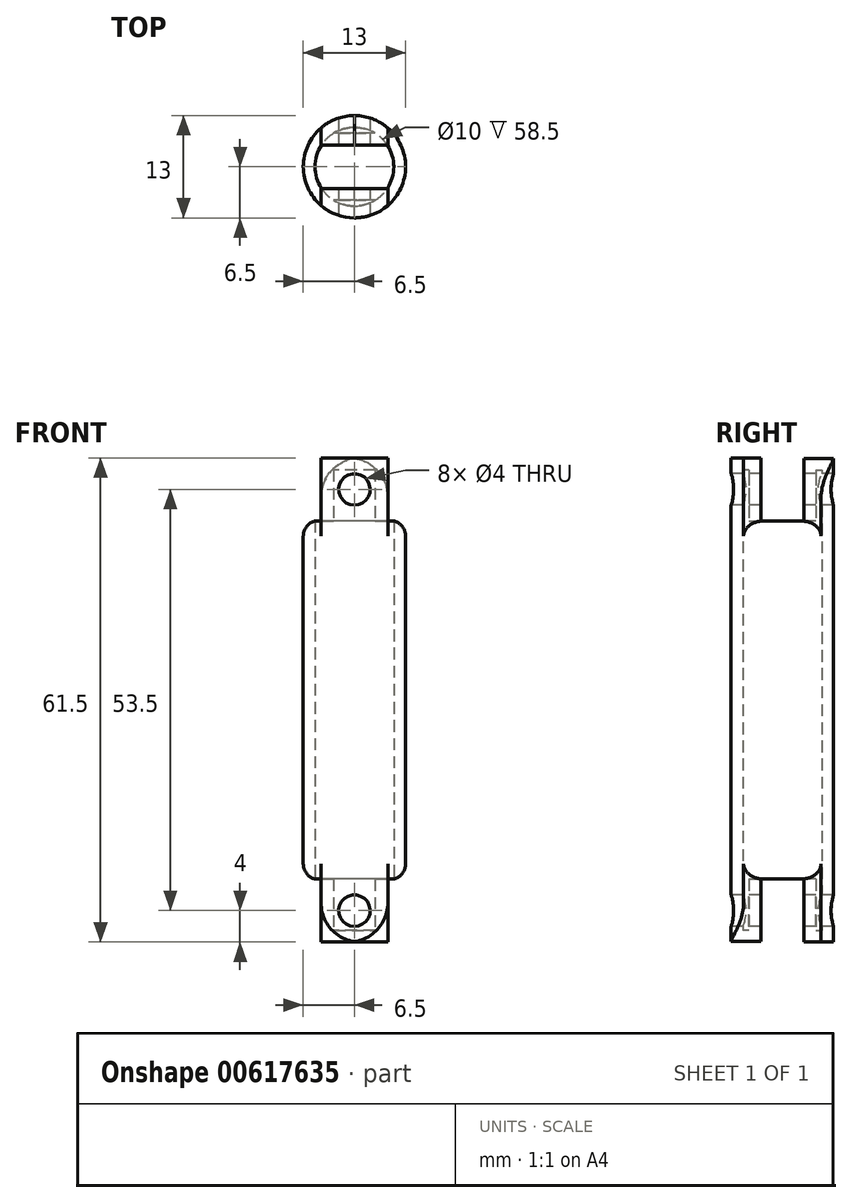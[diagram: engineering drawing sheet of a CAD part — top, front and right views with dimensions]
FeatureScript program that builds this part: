
annotation { "Feature Type Name" : "Feature", "Feature Type Description" : "" }
export const myFeature = defineFeature(function(context is Context, id is Id, definition is map)
    precondition{}
    {
        {
            var Q0;
            Q0=qCreatedBy(makeId("Top.planeOp"),FACE);
            var sketch = newSketch(context, id + "F0", { "sketchPlane" : qUnion([Q0])});
            skCircle(sketch, "E0", {"center": v(0, 0) * mm, "radius": 6.5 * mm});
            skSolve(sketch);
        }
        {
            var Q0;
            Q0=qSketchRegion(id+"F0",true);
            extrude(context, id + "F1", {"entities" : qUnion([Q0]), "depth" : 61.5 * mm, "offsetDistance" : 25 * mm});
        }
        {
            var Q0;
            Q0=makeQuery(id+"F1.opExtrude","CAP_FACE",FACE,{"disambiguationData":[OSD([sQuery(id+"F0.wireOp",EDGE,"E0")])],"isStart":true});
            var sketch = newSketch(context, id + "F2", { "sketchPlane" : qUnion([Q0])});
            skLineSegment(sketch, "E1.bottom", {"start": v(6, 2.75) * mm, "end": v(-6, 2.75) * mm});
            skLineSegment(sketch, "E1.top", {"start": v(6, -2.75) * mm, "end": v(-6, -2.75) * mm});
            skLineSegment(sketch, "E1.left", {"start": v(6, 2.75) * mm, "end": v(6, -2.75) * mm});
            skLineSegment(sketch, "E1.right", {"start": v(-6, 2.75) * mm, "end": v(-6, -2.75) * mm});
            skPoint(sketch, "E1.middle", {"position": v(0, 0) * mm});
            skLineSegment(sketch, "E2.bottom", {"start": v(-4.25, 5) * mm, "end": v(-7.75, 5) * mm});
            skLineSegment(sketch, "E2.top", {"start": v(-4.25, -5) * mm, "end": v(-7.75, -5) * mm});
            skLineSegment(sketch, "E2.left", {"start": v(-4.25, 5) * mm, "end": v(-4.25, -5) * mm});
            skLineSegment(sketch, "E2.right", {"start": v(-7.75, 5) * mm, "end": v(-7.75, -5) * mm});
            skPoint(sketch, "E2.middle", {"position": v(-6, 0) * mm});
            skLineSegment(sketch, "E3.bottom", {"start": v(7.75, 5) * mm, "end": v(4.25, 5) * mm});
            skLineSegment(sketch, "E3.top", {"start": v(7.75, -5) * mm, "end": v(4.25, -5) * mm});
            skLineSegment(sketch, "E3.left", {"start": v(7.75, 5) * mm, "end": v(7.75, -5) * mm});
            skLineSegment(sketch, "E3.right", {"start": v(4.25, 5) * mm, "end": v(4.25, -5) * mm});
            skPoint(sketch, "E3.middle", {"position": v(6, 0) * mm});
            skSolve(sketch);
        }
        {
            var Q0;
            Q0=qSketchRegion(id+"F2",true);
            extrude(context, id + "F3", {"entities" : qUnion([Q0]), "operationType" : NewBodyOperationType.REMOVE, "oppositeDirection" : true, "depth" : 8 * mm, "offsetDistance" : 25 * mm});
        }
        {
            var Q0;
            Q0=makeQuery(id+"F1.opExtrude","CAP_FACE",FACE,{"disambiguationData":[OSD([sQuery(id+"F0.wireOp",EDGE,"E0")])],"isStart":false});
            var sketch = newSketch(context, id + "F4", { "sketchPlane" : qUnion([Q0])});
            skLineSegment(sketch, "E4.bottom", {"start": v(6, 2.75) * mm, "end": v(-6, 2.75) * mm});
            skLineSegment(sketch, "E4.top", {"start": v(6, -2.75) * mm, "end": v(-6, -2.75) * mm});
            skLineSegment(sketch, "E4.left", {"start": v(6, 2.75) * mm, "end": v(6, -2.75) * mm});
            skLineSegment(sketch, "E4.right", {"start": v(-6, 2.75) * mm, "end": v(-6, -2.75) * mm});
            skPoint(sketch, "E4.middle", {"position": v(0, 0) * mm});
            skLineSegment(sketch, "E5.bottom", {"start": v(7.75, 5) * mm, "end": v(4.25, 5) * mm});
            skLineSegment(sketch, "E5.top", {"start": v(7.75, -5) * mm, "end": v(4.25, -5) * mm});
            skLineSegment(sketch, "E5.left", {"start": v(7.75, 5) * mm, "end": v(7.75, -5) * mm});
            skLineSegment(sketch, "E5.right", {"start": v(4.25, 5) * mm, "end": v(4.25, -5) * mm});
            skPoint(sketch, "E5.middle", {"position": v(6, 0) * mm});
            skLineSegment(sketch, "E6.bottom", {"start": v(-4.25, 5) * mm, "end": v(-7.75, 5) * mm});
            skLineSegment(sketch, "E6.top", {"start": v(-4.25, -5) * mm, "end": v(-7.75, -5) * mm});
            skLineSegment(sketch, "E6.left", {"start": v(-4.25, 5) * mm, "end": v(-4.25, -5) * mm});
            skLineSegment(sketch, "E6.right", {"start": v(-7.75, 5) * mm, "end": v(-7.75, -5) * mm});
            skPoint(sketch, "E6.middle", {"position": v(-6, 0) * mm});
            skSolve(sketch);
        }
        {
            var Q0;
            Q0=qSketchRegion(id+"F4",true);
            extrude(context, id + "F5", {"entities" : qUnion([Q0]), "operationType" : NewBodyOperationType.REMOVE, "oppositeDirection" : true, "depth" : 8 * mm, "offsetDistance" : 25 * mm});
        }
        {
            var Q0;
            Q0=makeQuery(id+"F3.boolean.opBoolean","COPY",FACE,{"derivedFrom":makeQuery(id+"F3.opExtrude","SWEPT_FACE",FACE,{"disambiguationData":[OSD([sQuery(id+"F2.wireOp",EDGE,"E1.top")])]})});
            var sketch = newSketch(context, id + "F6", { "sketchPlane" : qUnion([Q0])});
            skCircle(sketch, "E7", {"center": v(0, 4) * mm, "radius": 2 * mm});
            skPoint(sketch, "E7.centerSnap0", {"position": v(-4.18, 4) * mm});
            skSolve(sketch);
        }
        {
            var Q0;
            Q0=makeQuery(id+"F3.boolean.opBoolean","COPY",FACE,{"derivedFrom":makeQuery(id+"F3.opExtrude","CAP_FACE",FACE,{"disambiguationData":[OSD([sQuery(id+"F2.wireOp",EDGE,"E1.bottom"),sQuery(id+"F2.wireOp",EDGE,"E1.top"),sQuery(id+"F2.wireOp",EDGE,"E2.bottom"),sQuery(id+"F2.wireOp",EDGE,"E2.top"),sQuery(id+"F2.wireOp",EDGE,"E2.left"),sQuery(id+"F2.wireOp",EDGE,"E2.right"),sQuery(id+"F2.wireOp",EDGE,"E3.bottom"),sQuery(id+"F2.wireOp",EDGE,"E3.top"),sQuery(id+"F2.wireOp",EDGE,"E3.left"),sQuery(id+"F2.wireOp",EDGE,"E3.right")])],"isStart":false})});
            var Q1;
            Q1=makeQuery(id+"F5.boolean.opBoolean","COPY",FACE,{"derivedFrom":makeQuery(id+"F5.opExtrude","CAP_FACE",FACE,{"disambiguationData":[OSD([sQuery(id+"F4.wireOp",EDGE,"E4.bottom"),sQuery(id+"F4.wireOp",EDGE,"E4.top"),sQuery(id+"F4.wireOp",EDGE,"E5.bottom"),sQuery(id+"F4.wireOp",EDGE,"E5.top"),sQuery(id+"F4.wireOp",EDGE,"E5.left"),sQuery(id+"F4.wireOp",EDGE,"E5.right"),sQuery(id+"F4.wireOp",EDGE,"E6.bottom"),sQuery(id+"F4.wireOp",EDGE,"E6.top"),sQuery(id+"F4.wireOp",EDGE,"E6.left"),sQuery(id+"F4.wireOp",EDGE,"E6.right")])],"isStart":false})});
            shell(context, id + "F7", {"entities" : qUnion([Q0, Q1]), "thickness" : 1.5 * mm});
        }
        {
            var Q0;
            Q0=makeQuery(id+"F5.boolean.opBoolean","COPY",FACE,{"derivedFrom":makeQuery(id+"F5.opExtrude","SWEPT_FACE",FACE,{"disambiguationData":[OSD([sQuery(id+"F4.wireOp",EDGE,"E4.bottom")])]})});
            var sketch = newSketch(context, id + "F8", { "sketchPlane" : qUnion([Q0])});
            skCircle(sketch, "E8", {"center": v(0, 57.5) * mm, "radius": 2 * mm});
            skPoint(sketch, "E8.centerSnap0", {"position": v(-4.25, 57.5) * mm});
            skPoint(sketch, "E9", {"position": v(6.83, 57.5) * mm});
            skSolve(sketch);
        }
        {
            var Q0;
            Q0=qSketchRegion(id+"F8",true);
            extrude(context, id + "F9", {"entities" : qUnion([Q0]), "operationType" : NewBodyOperationType.REMOVE, "oppositeDirection" : true, "depth" : 25 * mm, "offsetDistance" : 25 * mm, "hasSecondDirection" : true, "secondDirectionOppositeDirection" : false, "secondDirectionDepth" : 25 * mm});
        }
        {
            var Q0;
            Q0=qSketchRegion(id+"F6",true);
            extrude(context, id + "F10", {"entities" : qUnion([Q0]), "operationType" : NewBodyOperationType.REMOVE, "oppositeDirection" : true, "depth" : 25 * mm, "offsetDistance" : 25 * mm, "hasSecondDirection" : true, "secondDirectionOppositeDirection" : false, "secondDirectionDepth" : 25 * mm});
        }
        {
            var Q0;
            Q0=makeQuery(id+"F5.boolean.opBoolean","COPY",FACE,{"derivedFrom":makeQuery(id+"F5.opExtrude","SWEPT_FACE",FACE,{"disambiguationData":[OSD([sQuery(id+"F4.wireOp",EDGE,"E4.bottom")])]})});
            var sketch = newSketch(context, id + "F11", { "sketchPlane" : qUnion([Q0])});
            skCircle(sketch, "E10", {"center": v(0, 57.5) * mm, "radius": 5 * mm});
            skSolve(sketch);
        }
        {
            var Q0;
            Q0=qSketchRegion(id+"F11",true);
            extrude(context, id + "F12", {"entities" : qUnion([Q0]), "operationType" : NewBodyOperationType.REMOVE, "depth" : 5.5 * mm, "offsetDistance" : 25 * mm});
        }
        {
            var Q0;
            Q0=makeQuery(id+"F3.boolean.opBoolean","COPY",FACE,{"derivedFrom":makeQuery(id+"F3.opExtrude","SWEPT_FACE",FACE,{"disambiguationData":[OSD([sQuery(id+"F2.wireOp",EDGE,"E1.top")])]})});
            var sketch = newSketch(context, id + "F13", { "sketchPlane" : qUnion([Q0])});
            skCircle(sketch, "E11", {"center": v(0, 4) * mm, "radius": 5 * mm});
            skSolve(sketch);
        }
        {
            var Q0;
            Q0=qSketchRegion(id+"F13",true);
            extrude(context, id + "F14", {"entities" : qUnion([Q0]), "operationType" : NewBodyOperationType.REMOVE, "depth" : 5.5 * mm, "offsetDistance" : 25 * mm});
        }
        {
            var Q0;
            {var subQ0=sQuery(id+"F4.wireOp",EDGE,"E5.right");Q0=makeQuery(id+"F5.boolean.opBoolean","COPY",EDGE,{"derivedFrom":makeQuery(id+"F5.opExtrude","CAP_EDGE",EDGE,{"disambiguationData":[OSD([subQ0]),TDD([makeQuery(id+"F4.imprint","IMPRINT",EDGE,{"disambiguationData":[TD([[makeQuery(id+"F4.imprint","INTERSECT",VERTEX,{"derivedFrom":[sQuery(id+"F4.wireOp",EDGE,"E4.top"),subQ0]}),-1.0]])],"derivedFrom":subQ0}),makeQuery(id+"F4.imprint","IMPRINT",EDGE,{"disambiguationData":[TD([[makeQuery(id+"F4.imprint","INTERSECT",VERTEX,{"derivedFrom":[sQuery(id+"F4.wireOp",EDGE,"E5.top"),subQ0]}),1.0]])],"derivedFrom":subQ0})])],"isStart":true})});}
            var Q1;
            {var subQ0=sQuery(id+"F4.wireOp",EDGE,"E5.right");Q1=makeQuery(id+"F5.boolean.opBoolean","COPY",EDGE,{"derivedFrom":makeQuery(id+"F5.opExtrude","CAP_EDGE",EDGE,{"disambiguationData":[OSD([subQ0]),TDD([makeQuery(id+"F4.imprint","IMPRINT",EDGE,{"disambiguationData":[TD([[makeQuery(id+"F4.imprint","INTERSECT",VERTEX,{"derivedFrom":[sQuery(id+"F4.wireOp",EDGE,"E5.bottom"),subQ0]}),-1.0]])],"derivedFrom":subQ0}),makeQuery(id+"F4.imprint","IMPRINT",EDGE,{"disambiguationData":[TD([[makeQuery(id+"F4.imprint","INTERSECT",VERTEX,{"derivedFrom":[sQuery(id+"F4.wireOp",EDGE,"E4.bottom"),subQ0]}),1.0]])],"derivedFrom":subQ0})])],"isStart":true})});}
            var Q2;
            {var subQ0=sQuery(id+"F4.wireOp",EDGE,"E6.left");Q2=makeQuery(id+"F5.boolean.opBoolean","COPY",EDGE,{"derivedFrom":makeQuery(id+"F5.opExtrude","CAP_EDGE",EDGE,{"disambiguationData":[OSD([subQ0]),TDD([makeQuery(id+"F4.imprint","IMPRINT",EDGE,{"disambiguationData":[TD([[makeQuery(id+"F4.imprint","INTERSECT",VERTEX,{"derivedFrom":[sQuery(id+"F4.wireOp",EDGE,"E4.top"),subQ0]}),-1.0]])],"derivedFrom":subQ0}),makeQuery(id+"F4.imprint","IMPRINT",EDGE,{"disambiguationData":[TD([[makeQuery(id+"F4.imprint","INTERSECT",VERTEX,{"derivedFrom":[sQuery(id+"F4.wireOp",EDGE,"E6.top"),subQ0]}),1.0]])],"derivedFrom":subQ0})])],"isStart":true})});}
            var Q3;
            {var subQ0=sQuery(id+"F4.wireOp",EDGE,"E6.left");Q3=makeQuery(id+"F5.boolean.opBoolean","COPY",EDGE,{"derivedFrom":makeQuery(id+"F5.opExtrude","CAP_EDGE",EDGE,{"disambiguationData":[OSD([subQ0]),TDD([makeQuery(id+"F4.imprint","IMPRINT",EDGE,{"disambiguationData":[TD([[makeQuery(id+"F4.imprint","INTERSECT",VERTEX,{"derivedFrom":[sQuery(id+"F4.wireOp",EDGE,"E6.bottom"),subQ0]}),-1.0]])],"derivedFrom":subQ0}),makeQuery(id+"F4.imprint","IMPRINT",EDGE,{"disambiguationData":[TD([[makeQuery(id+"F4.imprint","INTERSECT",VERTEX,{"derivedFrom":[sQuery(id+"F4.wireOp",EDGE,"E4.bottom"),subQ0]}),1.0]])],"derivedFrom":subQ0})])],"isStart":true})});}
            var Q4;
            {var subQ0=sQuery(id+"F2.wireOp",EDGE,"E2.left");Q4=makeQuery(id+"F3.boolean.opBoolean","COPY",EDGE,{"derivedFrom":makeQuery(id+"F3.opExtrude","CAP_EDGE",EDGE,{"disambiguationData":[OSD([subQ0]),TDD([makeQuery(id+"F2.imprint","IMPRINT",EDGE,{"disambiguationData":[TD([[makeQuery(id+"F2.imprint","INTERSECT",VERTEX,{"derivedFrom":[sQuery(id+"F2.wireOp",EDGE,"E1.top"),subQ0]}),-1.0]])],"derivedFrom":subQ0}),makeQuery(id+"F2.imprint","IMPRINT",EDGE,{"disambiguationData":[TD([[makeQuery(id+"F2.imprint","INTERSECT",VERTEX,{"derivedFrom":[sQuery(id+"F2.wireOp",EDGE,"E2.top"),subQ0]}),1.0]])],"derivedFrom":subQ0})])],"isStart":true})});}
            var Q5;
            {var subQ0=sQuery(id+"F2.wireOp",EDGE,"E3.right");Q5=makeQuery(id+"F3.boolean.opBoolean","COPY",EDGE,{"derivedFrom":makeQuery(id+"F3.opExtrude","CAP_EDGE",EDGE,{"disambiguationData":[OSD([subQ0]),TDD([makeQuery(id+"F2.imprint","IMPRINT",EDGE,{"disambiguationData":[TD([[makeQuery(id+"F2.imprint","INTERSECT",VERTEX,{"derivedFrom":[sQuery(id+"F2.wireOp",EDGE,"E1.top"),subQ0]}),-1.0]])],"derivedFrom":subQ0}),makeQuery(id+"F2.imprint","IMPRINT",EDGE,{"disambiguationData":[TD([[makeQuery(id+"F2.imprint","INTERSECT",VERTEX,{"derivedFrom":[sQuery(id+"F2.wireOp",EDGE,"E3.top"),subQ0]}),1.0]])],"derivedFrom":subQ0})])],"isStart":true})});}
            var Q6;
            {var subQ0=sQuery(id+"F2.wireOp",EDGE,"E3.right");Q6=makeQuery(id+"F3.boolean.opBoolean","COPY",EDGE,{"derivedFrom":makeQuery(id+"F3.opExtrude","CAP_EDGE",EDGE,{"disambiguationData":[OSD([subQ0]),TDD([makeQuery(id+"F2.imprint","IMPRINT",EDGE,{"disambiguationData":[TD([[makeQuery(id+"F2.imprint","INTERSECT",VERTEX,{"derivedFrom":[sQuery(id+"F2.wireOp",EDGE,"E3.bottom"),subQ0]}),-1.0]])],"derivedFrom":subQ0}),makeQuery(id+"F2.imprint","IMPRINT",EDGE,{"disambiguationData":[TD([[makeQuery(id+"F2.imprint","INTERSECT",VERTEX,{"derivedFrom":[sQuery(id+"F2.wireOp",EDGE,"E1.bottom"),subQ0]}),1.0]])],"derivedFrom":subQ0})])],"isStart":true})});}
            var Q7;
            {var subQ0=sQuery(id+"F2.wireOp",EDGE,"E2.left");Q7=makeQuery(id+"F3.boolean.opBoolean","COPY",EDGE,{"derivedFrom":makeQuery(id+"F3.opExtrude","CAP_EDGE",EDGE,{"disambiguationData":[OSD([subQ0]),TDD([makeQuery(id+"F2.imprint","IMPRINT",EDGE,{"disambiguationData":[TD([[makeQuery(id+"F2.imprint","INTERSECT",VERTEX,{"derivedFrom":[sQuery(id+"F2.wireOp",EDGE,"E2.bottom"),subQ0]}),-1.0]])],"derivedFrom":subQ0}),makeQuery(id+"F2.imprint","IMPRINT",EDGE,{"disambiguationData":[TD([[makeQuery(id+"F2.imprint","INTERSECT",VERTEX,{"derivedFrom":[sQuery(id+"F2.wireOp",EDGE,"E1.bottom"),subQ0]}),1.0]])],"derivedFrom":subQ0})])],"isStart":true})});}
            fillet(context, id + "F15", {"entities" : qUnion([Q0, Q1, Q2, Q3, Q4, Q5, Q6, Q7]), "radius" : 5 * mm, "tangentPropagation" : true, "allowEdgeOverflow" : false});
        }
        {
            var Q0;
            Q0=makeQuery(id+"F5.boolean.opBoolean","INTERSECT",EDGE,{"disambiguationData":[OD(0.0)],"derivedFrom":[makeQuery(id+"F1.opExtrude","SWEPT_FACE",FACE,{"disambiguationData":[OSD([sQuery(id+"F0.wireOp",EDGE,"E0")])]}),makeQuery(id+"F5.opExtrude","CAP_FACE",FACE,{"disambiguationData":[OSD([sQuery(id+"F4.wireOp",EDGE,"E4.bottom"),sQuery(id+"F4.wireOp",EDGE,"E4.top"),sQuery(id+"F4.wireOp",EDGE,"E5.bottom"),sQuery(id+"F4.wireOp",EDGE,"E5.top"),sQuery(id+"F4.wireOp",EDGE,"E5.left"),sQuery(id+"F4.wireOp",EDGE,"E5.right"),sQuery(id+"F4.wireOp",EDGE,"E6.bottom"),sQuery(id+"F4.wireOp",EDGE,"E6.top"),sQuery(id+"F4.wireOp",EDGE,"E6.left"),sQuery(id+"F4.wireOp",EDGE,"E6.right")])],"isStart":false})]});
            var Q1;
            Q1=makeQuery(id+"F3.boolean.opBoolean","INTERSECT",EDGE,{"disambiguationData":[OD(1.0)],"derivedFrom":[makeQuery(id+"F1.opExtrude","SWEPT_FACE",FACE,{"disambiguationData":[OSD([sQuery(id+"F0.wireOp",EDGE,"E0")])]}),makeQuery(id+"F3.opExtrude","CAP_FACE",FACE,{"disambiguationData":[OSD([sQuery(id+"F2.wireOp",EDGE,"E1.bottom"),sQuery(id+"F2.wireOp",EDGE,"E1.top"),sQuery(id+"F2.wireOp",EDGE,"E2.bottom"),sQuery(id+"F2.wireOp",EDGE,"E2.top"),sQuery(id+"F2.wireOp",EDGE,"E2.left"),sQuery(id+"F2.wireOp",EDGE,"E2.right"),sQuery(id+"F2.wireOp",EDGE,"E3.bottom"),sQuery(id+"F2.wireOp",EDGE,"E3.top"),sQuery(id+"F2.wireOp",EDGE,"E3.left"),sQuery(id+"F2.wireOp",EDGE,"E3.right")])],"isStart":false})]});
            fillet(context, id + "F16", {"entities" : qUnion([Q0, Q1]), "radius" : 2 * mm, "tangentPropagation" : true, "allowEdgeOverflow" : false});
        }
    });
